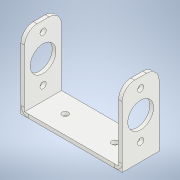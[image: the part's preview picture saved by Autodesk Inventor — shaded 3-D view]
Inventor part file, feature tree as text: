
AUTODESK INVENTOR PART (.ipt)
format: ipt  version: 2022 (Build 260153000, 153)  size: 221,696 bytes
history: native  units: in
note: dims shown in document units (in); Inventor stores cm internally (conversion verified against a paired STEP export)
features: sketch x5, sheet_metal_op x4, projected_geometry x4, hole x3, extrude x2, other x2, fillet x1
ambient origin geometry x8: Origin, YZ Plane, XZ Plane, XY Plane, X Axis, Y Axis, Z Axis, Center Point
bodies: Body1 (feature_tree)
feature tree (21):
  sheet_metal_op  "Face1"
  sheet_metal_op  "Flange1"
  sketch  "Sketch5"  dims[d14=0.16in d15=0.08in]
  hole  "Hole1"  [1 undecoded]
  hole  "Hole2"  [1 undecoded]
  fillet  "Fillet1"  Radius=0.04in
  hole  "Hole3"  [1 undecoded]
  sketch  "Sketch7"  dims[d20=0.08in d21=0.08in d22=0.4921in d23=0.4921in d24=0.1339in d25=0.2362in d26=0.2559in d27=0.1181in d28=0.6181in d29=0.08in d30=0.8108in d31=0.5512in d32=0.2362in d33=0.1575in d34=0.0787in d35=90.0deg d36=0.315in d37=0.8108in d38=0.2662in d39=0.3937in d40=0.1339in d41=0.2362in d42=0.2559in d43=0.1181in d44=90.0deg d45=0.315in d46=0.8108in d47=0.0in d48=0.0in d49=0.3937in d50=0.0in d7=0.0197in d8=1.9685in]
  extrude  "Extrusion3"  Depth=0.08in
  extrude  "Extrusion4"  Depth=0.08in
  sketch  "Sketch3"  dims[d9=2.1654in d10=0.7874in]
  other  "Plate1"
  sketch  "Sketch4"  dims[d11=0.08in d12=0.08in d13=0.04in]
  other  "Plate2"
  sheet_metal_op  "Bend1"
  sheet_metal_op  "Corner1"
  projected_geometry  "Projected Loop3"
  sketch  "Sketch6"  dims[d16=1.5748in d17=90.0deg d18=0.08in d19=0.32in]
  projected_geometry  "Projected Loop4"
  projected_geometry  "Projected Loop5"
  projected_geometry  "Projected Loop6"
note: 3 required parameter values undecoded (feature->parameter linkage not recoverable at this tier; creation-order binding heuristic only, values carry confidence <= 0.55)
